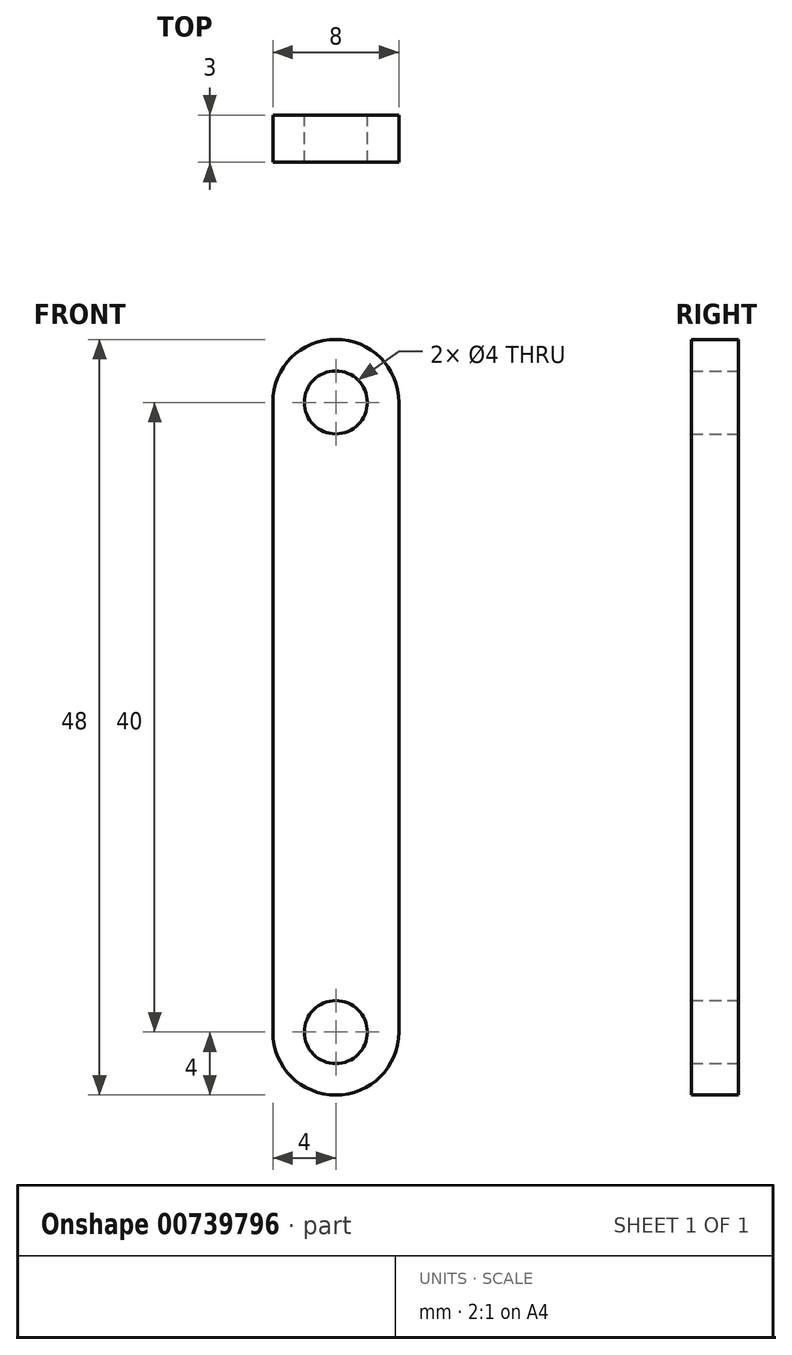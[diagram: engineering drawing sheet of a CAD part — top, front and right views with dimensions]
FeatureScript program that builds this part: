
annotation { "Feature Type Name" : "Feature", "Feature Type Description" : "" }
export const myFeature = defineFeature(function(context is Context, id is Id, definition is map)
    precondition{}
    {
        {
            var Q0;
            Q0=qCreatedBy(makeId("Front.planeOp"),FACE);
            var sketch = newSketch(context, id + "F0", { "sketchPlane" : qUnion([Q0])});
            skLineSegment(sketch, "E0.bottom", {"start": v(4, 20) * mm, "end": v(-4, 20) * mm, "construction": true});
            skLineSegment(sketch, "E0.top", {"start": v(4, -20) * mm, "end": v(-4, -20) * mm, "construction": true});
            skLineSegment(sketch, "E0.left", {"start": v(4, 20) * mm, "end": v(4, -20) * mm});
            skLineSegment(sketch, "E0.right", {"start": v(-4, 20) * mm, "end": v(-4, -20) * mm});
            skPoint(sketch, "E0.middle", {"position": v(0, 0) * mm});
            skArc(sketch, "E1", {"start": v(4, 20) * mm, "mid": v(0, 24) * mm, "end": v(-4, 20) * mm});
            skArc(sketch, "E2", {"start": v(-4, -20) * mm, "mid": v(0, -24) * mm, "end": v(4, -20) * mm});
            skCircle(sketch, "E3", {"center": v(0, 20) * mm, "radius": 2 * mm});
            skCircle(sketch, "E4", {"center": v(0, -20) * mm, "radius": 2 * mm});
            skSolve(sketch);
        }
        {
            var Q0;
            Q0 = qSketchRegion(id + "F0", true);
            extrude(context, id + "F1", {"entities" : qUnion([Q0]), "depth" : 3 * mm, "offsetDistance" : 25 * mm});
        }
    });
